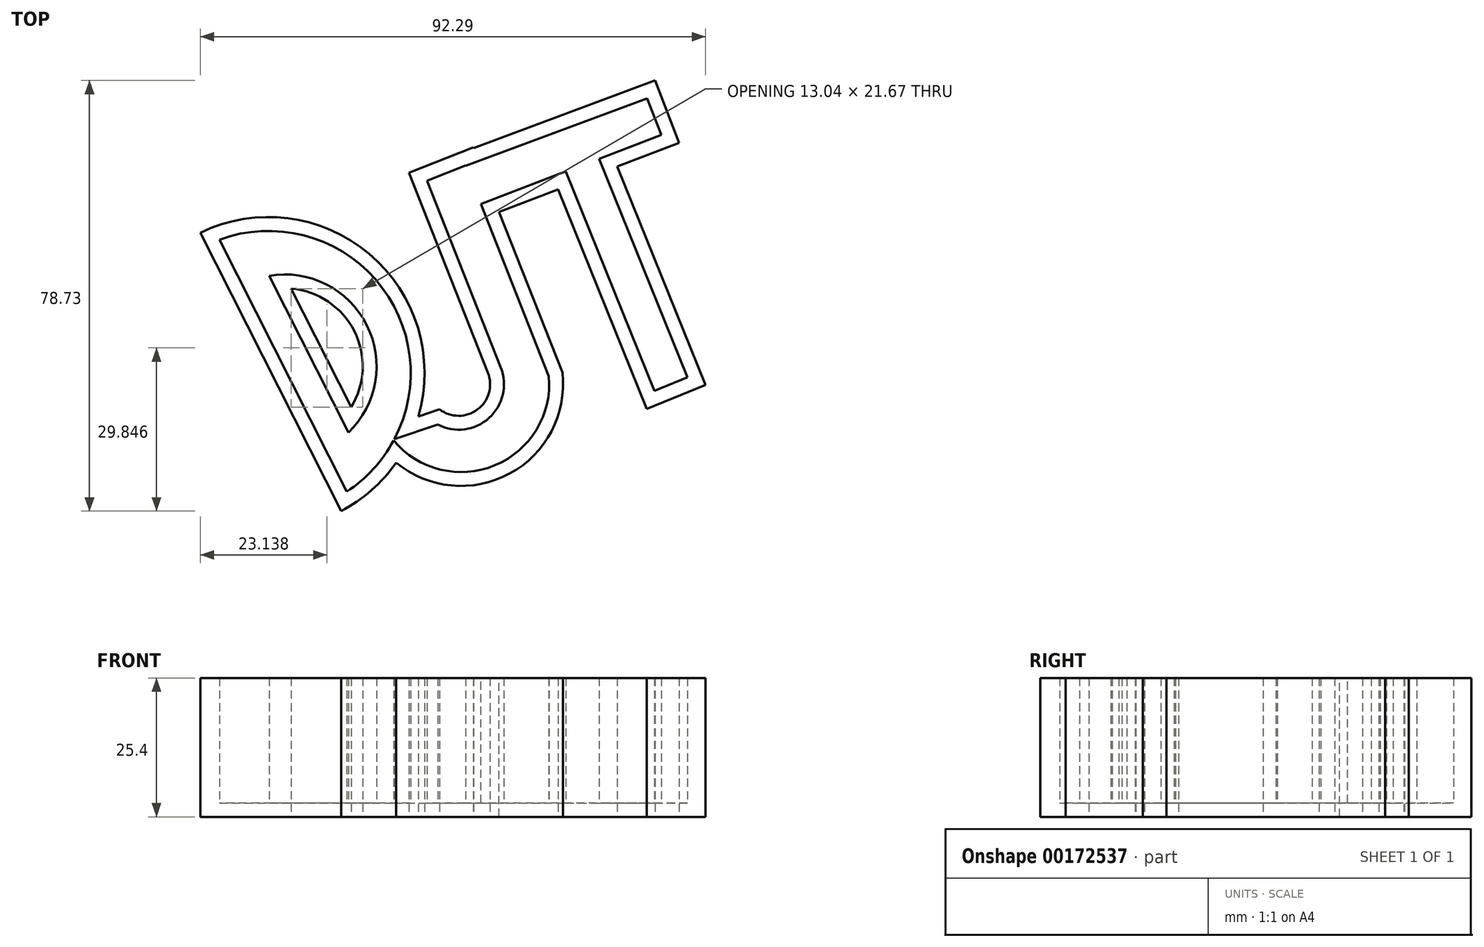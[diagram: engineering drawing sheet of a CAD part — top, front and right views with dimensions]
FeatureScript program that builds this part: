
annotation { "Feature Type Name" : "Feature", "Feature Type Description" : "" }
export const myFeature = defineFeature(function(context is Context, id is Id, definition is map)
    precondition{}
    {
        {
            var Q0;
            Q0=qCreatedBy(makeId("Top.planeOp"),FACE);
            var sketch = newSketch(context, id + "F0", { "sketchPlane" : qUnion([Q0])});
            skLineSegment(sketch, "E0", {"start": v(6.17, 55.32) * mm, "end": v(22.47, 14.08) * mm});
            skArc(sketch, "E1", {"start": v(-12.47, 3.2) * mm, "mid": v(9.48, -5.75) * mm, "end": v(22.47, 14.08) * mm});
            skLineSegment(sketch, "E2", {"start": v(6.17, 55.32) * mm, "end": v(-5.6, 50.66) * mm});
            skLineSegment(sketch, "E3", {"start": v(-5.6, 50.66) * mm, "end": v(8.84, 14.1) * mm});
            skArc(sketch, "E4", {"start": v(0, 7.4) * mm, "mid": v(6.97, 7.4) * mm, "end": v(8.84, 14.1) * mm});
            skLineSegment(sketch, "E5", {"start": v(-12.47, 3.2) * mm, "end": v(0, 7.4) * mm});
            skSolve(sketch);
        }
        {
            var Q0;
            Q0=makeQuery(id+"F0.imprint","IMPRINT",FACE,{"disambiguationData":[TD([[makeQuery(id+"F0.imprint","IMPRINT",EDGE,{"derivedFrom":sQuery(id+"F0.wireOp",EDGE,"E0")}),-1.0]])]});
            extrude(context, id + "F1", {"entities" : qUnion([Q0]), "depth" : 25.4 * mm});
        }
        {
            var Q0;
            Q0=qCreatedBy(makeId("Top.planeOp"),FACE);
            var sketch = newSketch(context, id + "F2", { "sketchPlane" : qUnion([Q0])});
            skLineSegment(sketch, "E6", {"start": v(-43.7, 39.71) * mm, "end": v(-18, -11.2) * mm});
            skArc(sketch, "E7", {"start": v(-18, -11.2) * mm, "mid": v(-5.79, 26.9) * mm, "end": v(-43.7, 39.71) * mm});
            skLineSegment(sketch, "E8", {"start": v(-27.08, 29.48) * mm, "end": v(-16.14, 7.81) * mm});
            skArc(sketch, "E9", {"start": v(-16.14, 7.81) * mm, "mid": v(-15.56, 21.7) * mm, "end": v(-27.08, 29.48) * mm});
            skSolve(sketch);
        }
        {
            var Q0;
            Q0=makeQuery(id+"F2.imprint","IMPRINT",FACE,{"disambiguationData":[TD([[makeQuery(id+"F2.imprint","IMPRINT",EDGE,{"derivedFrom":sQuery(id+"F2.wireOp",EDGE,"E6")}),1.0]])]});
            extrude(context, id + "F3", {"entities" : qUnion([Q0]), "operationType" : NewBodyOperationType.ADD, "depth" : 25.4 * mm});
        }
        {
            var Q0;
            Q0=qCreatedBy(makeId("Top.planeOp"),FACE);
            var sketch = newSketch(context, id + "F4", { "sketchPlane" : qUnion([Q0])});
            skLineSegment(sketch, "E10", {"start": v(5.96, 55.1) * mm, "end": v(10.47, 43.35) * mm});
            skLineSegment(sketch, "E11", {"start": v(10.47, 43.35) * mm, "end": v(43.78, 56.12) * mm});
            skLineSegment(sketch, "E12", {"start": v(21.65, 47.64) * mm, "end": v(37.86, 7.51) * mm});
            skLineSegment(sketch, "E13", {"start": v(37.86, 7.51) * mm, "end": v(48.59, 11.85) * mm});
            skLineSegment(sketch, "E14", {"start": v(48.59, 11.85) * mm, "end": v(32.45, 51.78) * mm});
            skLineSegment(sketch, "E15", {"start": v(43.78, 56.12) * mm, "end": v(39.4, 67.53) * mm});
            skLineSegment(sketch, "E16", {"start": v(39.4, 67.53) * mm, "end": v(5.96, 55.1) * mm});
            skSolve(sketch);
        }
        {
            var Q0;
            {var subQ3=sQuery(id+"F4.wireOp",EDGE,"E10");Q0=makeQuery(id+"F4.imprint","IMPRINT",FACE,{"disambiguationData":[TD([[makeQuery(id+"F4.imprint","IMPRINT",EDGE,{"derivedFrom":subQ3}),1.0]])]});}
            var Q1;
            {var subQ0=sQuery(id+"F4.wireOp",EDGE,"E12");Q1=makeQuery(id+"F4.imprint","IMPRINT",FACE,{"disambiguationData":[TD([[makeQuery(id+"F4.imprint","IMPRINT",EDGE,{"derivedFrom":subQ0}),1.0]])]});}
            extrude(context, id + "F5", {"entities" : qUnion([Q0, Q1]), "operationType" : NewBodyOperationType.ADD, "depth" : 25.4 * mm});
        }
        {
            var Q0;
            Q0=makeQuery(id+"F5.boolean.opBoolean","MERGE",FACE,{"derivedFrom":[makeQuery(id+"F3.boolean.opBoolean","MERGE",FACE,{"derivedFrom":[makeQuery(id+"F1.opExtrude","CAP_FACE",FACE,{"disambiguationData":[OSD([sQuery(id+"F0.wireOp",EDGE,"E0"),sQuery(id+"F0.wireOp",EDGE,"E1"),sQuery(id+"F0.wireOp",EDGE,"E2"),sQuery(id+"F0.wireOp",EDGE,"E3"),sQuery(id+"F0.wireOp",EDGE,"E4"),sQuery(id+"F0.wireOp",EDGE,"E5")])],"isStart":false}),makeQuery(id+"F3.opExtrude","CAP_FACE",FACE,{"disambiguationData":[OSD([sQuery(id+"F2.wireOp",EDGE,"E6"),sQuery(id+"F2.wireOp",EDGE,"E7"),sQuery(id+"F2.wireOp",EDGE,"E8"),sQuery(id+"F2.wireOp",EDGE,"E9")])],"isStart":false})]}),makeQuery(id+"F5.opExtrude","CAP_FACE",FACE,{"disambiguationData":[OSD([sQuery(id+"F4.wireOp",EDGE,"E10"),sQuery(id+"F4.wireOp",EDGE,"E11"),sQuery(id+"F4.wireOp",EDGE,"E12"),sQuery(id+"F4.wireOp",EDGE,"E13"),sQuery(id+"F4.wireOp",EDGE,"E14"),sQuery(id+"F4.wireOp",EDGE,"E15"),sQuery(id+"F4.wireOp",EDGE,"E16")])],"isStart":false})]});
            shell(context, id + "F6", {"entities" : qUnion([Q0]), "thickness" : 2.54 * mm});
        }
    });
